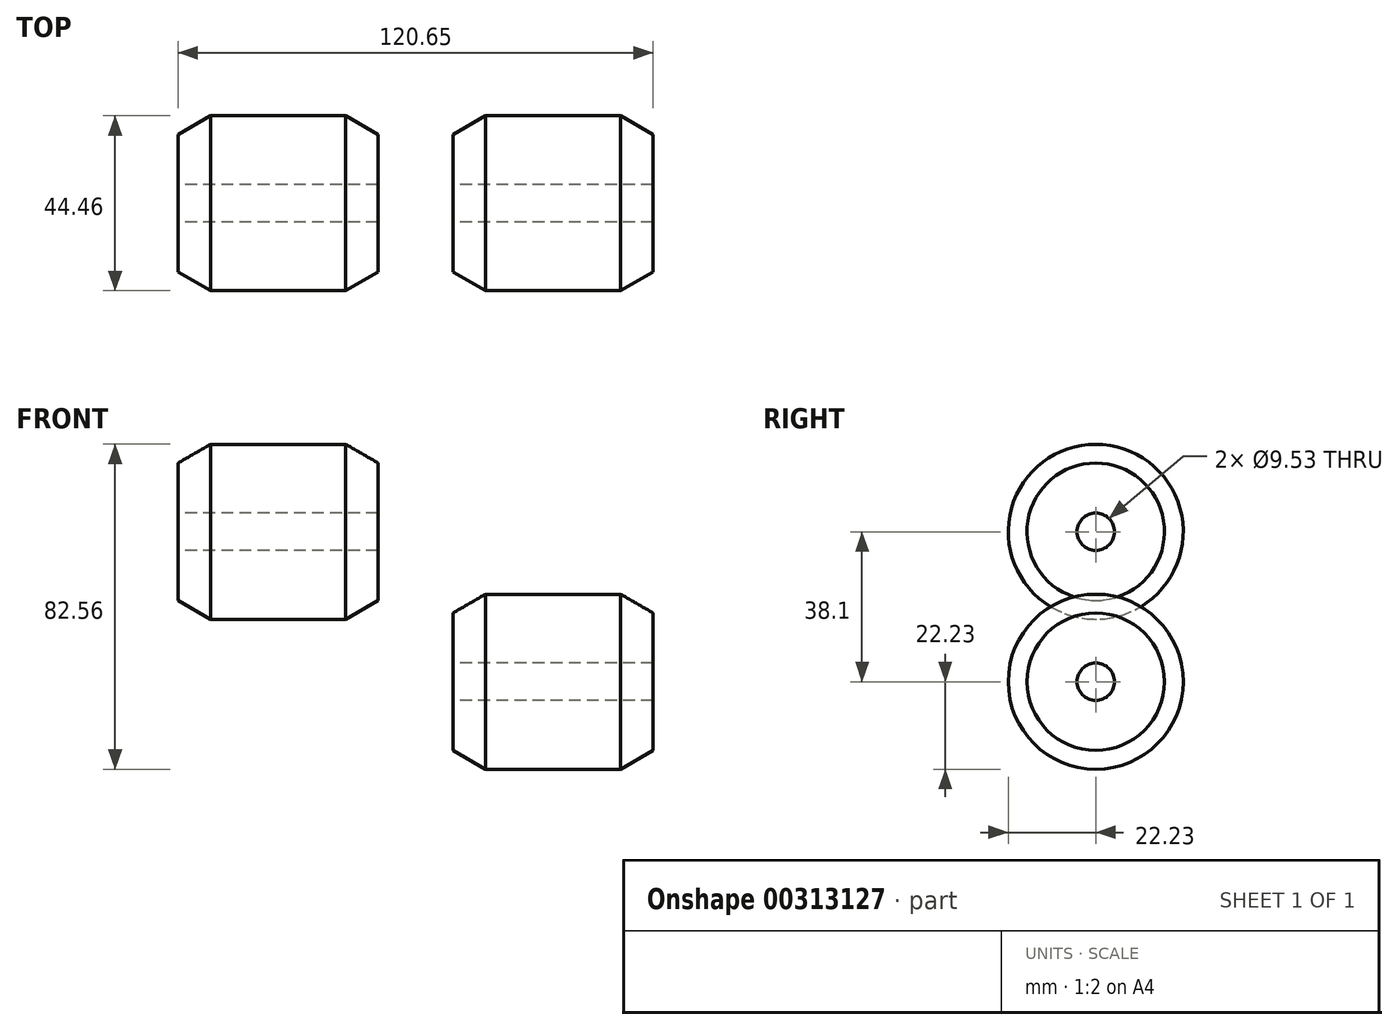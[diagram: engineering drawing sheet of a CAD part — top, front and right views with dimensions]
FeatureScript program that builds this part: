
annotation { "Feature Type Name" : "Feature", "Feature Type Description" : "" }
export const myFeature = defineFeature(function(context is Context, id is Id, definition is map)
    precondition{}
    {
        {
            var Q0;
            Q0=qCreatedBy(makeId("Front.planeOp"),FACE);
            var sketch = newSketch(context, id + "F0", { "sketchPlane" : qUnion([Q0])});
            skLineSegment(sketch, "E0", {"start": v(0, 0) * mm, "end": v(50.8, 0) * mm});
            skLineSegment(sketch, "E1", {"start": v(0, 0) * mm, "end": v(0, 17.46) * mm});
            skLineSegment(sketch, "E2", {"start": v(0, 17.46) * mm, "end": v(8.25, 22.23) * mm});
            skLineSegment(sketch, "E3", {"start": v(8.25, 22.23) * mm, "end": v(42.55, 22.23) * mm});
            skLineSegment(sketch, "E4", {"start": v(42.55, 22.23) * mm, "end": v(50.8, 17.46) * mm});
            skLineSegment(sketch, "E5", {"start": v(50.8, 17.46) * mm, "end": v(50.8, 0) * mm});
            skLineSegment(sketch, "E6", {"start": v(69.85, -38.1) * mm, "end": v(120.65, -38.1) * mm});
            skLineSegment(sketch, "E7", {"start": v(69.85, -38.1) * mm, "end": v(69.85, -20.64) * mm});
            skLineSegment(sketch, "E8", {"start": v(69.85, -20.64) * mm, "end": v(78.1, -15.87) * mm});
            skLineSegment(sketch, "E9", {"start": v(78.1, -15.87) * mm, "end": v(112.4, -15.87) * mm});
            skLineSegment(sketch, "E10", {"start": v(112.4, -15.87) * mm, "end": v(120.65, -20.64) * mm});
            skLineSegment(sketch, "E11", {"start": v(120.65, -20.64) * mm, "end": v(120.65, -38.1) * mm});
            skSolve(sketch);
        }
        {
            var Q0;
            Q0=makeQuery(id+"F0.imprint","IMPRINT",FACE,{"disambiguationData":[TD([[makeQuery(id+"F0.imprint","IMPRINT",EDGE,{"derivedFrom":sQuery(id+"F0.wireOp",EDGE,"E0")}),1.0]])]});
            var Q1;
            Q1=sQuery(id+"F0.wireOp",EDGE,"E0");
            revolve(context, id + "F1", {"entities" : qUnion([Q0]), "axis" : qUnion([Q1]), "revolveType" : RevolveType.FULL});
        }
        {
            var Q0;
            Q0=makeQuery(id+"F0.imprint","IMPRINT",FACE,{"disambiguationData":[TD([[makeQuery(id+"F0.imprint","IMPRINT",EDGE,{"derivedFrom":sQuery(id+"F0.wireOp",EDGE,"E6")}),1.0]])]});
            var Q1;
            Q1=sQuery(id+"F0.wireOp",EDGE,"E6");
            revolve(context, id + "F2", {"entities" : qUnion([Q0]), "axis" : qUnion([Q1]), "revolveType" : RevolveType.FULL});
        }
        {
            var Q0;
            Q0=makeQuery(id+"F1.opRevolve","SWEPT_FACE",FACE,{"disambiguationData":[OSD([sQuery(id+"F0.wireOp",EDGE,"E1")])]});
            var sketch = newSketch(context, id + "F3", { "sketchPlane" : qUnion([Q0])});
            skCircle(sketch, "E12", {"center": v(0, 0) * mm, "radius": 4.76 * mm});
            skCircle(sketch, "E13", {"center": v(0, -38.1) * mm, "radius": 4.76 * mm});
            skSolve(sketch);
        }
        {
            var Q0;
            Q0 = qSketchRegion(id + "F3", true);
            extrude(context, id + "F4", {"entities" : qUnion([Q0]), "operationType" : NewBodyOperationType.REMOVE, "endBound" : BoundingType.THROUGH_ALL, "oppositeDirection" : true, "depth" : 25.4 * mm});
        }
    });
